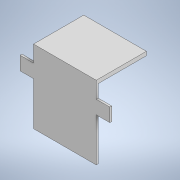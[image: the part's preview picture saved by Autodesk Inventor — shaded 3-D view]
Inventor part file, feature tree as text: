
AUTODESK INVENTOR PART (.ipt)
format: ipt  version: 2020.2 (Build 242310000, 310)  size: 111,616 bytes
history: native  units: mm
features: extrude x2, sketch x1
ambient origin geometry x8: Origin, YZ Plane, XZ Plane, XY Plane, X Axis, Y Axis, Z Axis, Center Point
bodies: Solid1 (feature_tree)
feature tree (3):
  sketch  "Sketch1"  dims[d0=32.48mm d1=36.0mm d2=22.48mm d3=7.0mm d4=90.0deg d5=7.0mm d6=7.0mm d7=2.0mm d8=1.0mm d9=0.0mm d10=25.0mm d11=0.0mm]
  extrude  "Extrusion1"  Depth=36.0mm
  extrude  "Extrusion2"  Depth=22.48mm
